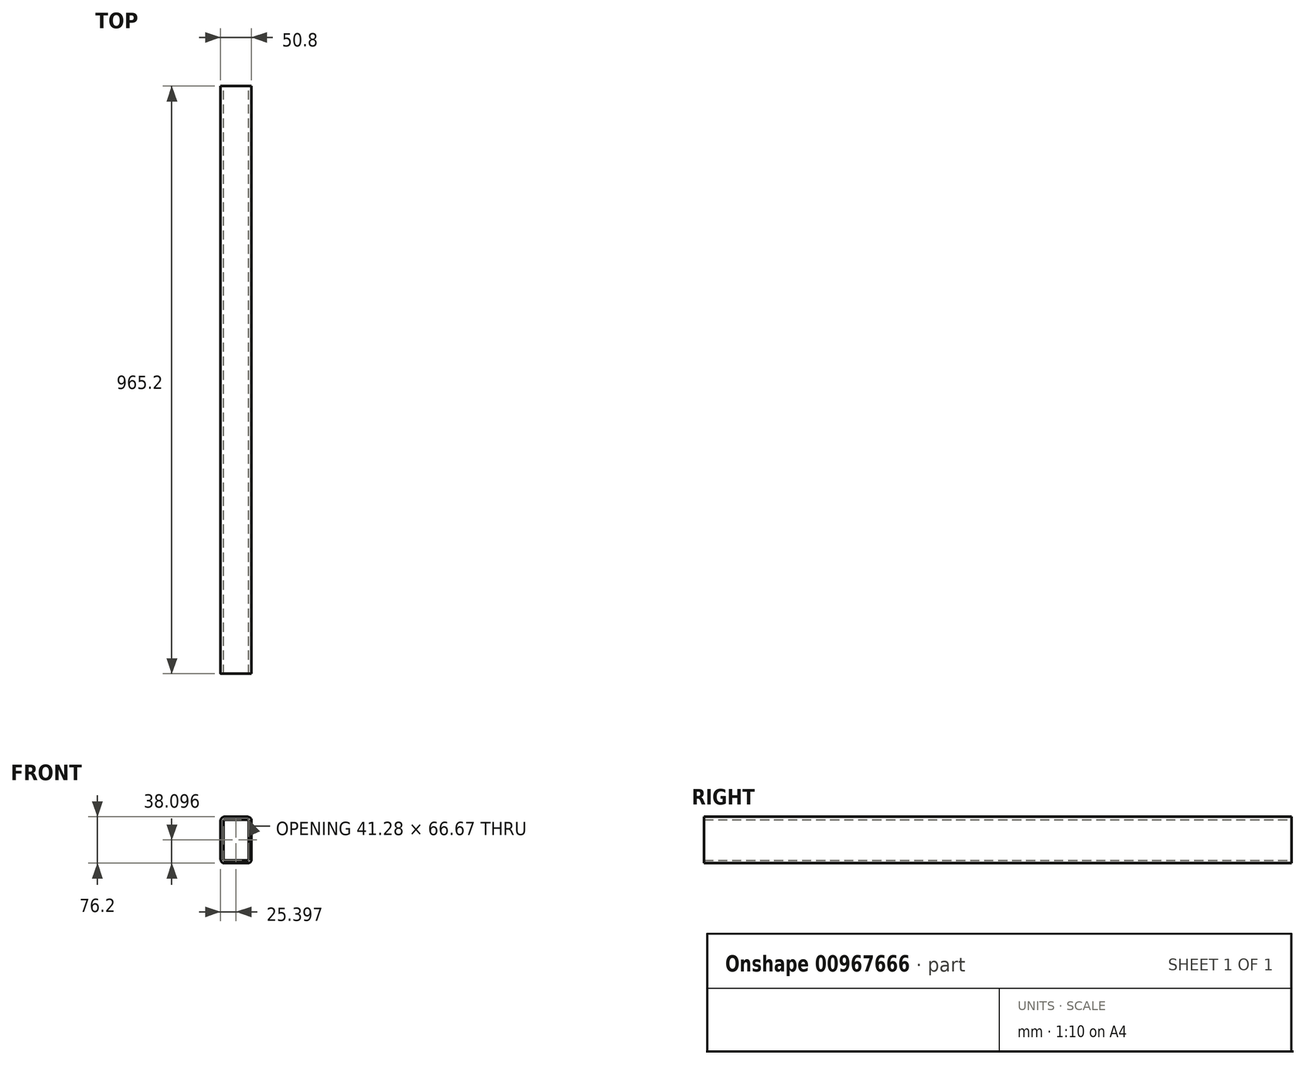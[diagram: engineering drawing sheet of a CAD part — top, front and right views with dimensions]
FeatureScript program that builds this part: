
annotation { "Feature Type Name" : "Feature", "Feature Type Description" : "" }
export const myFeature = defineFeature(function(context is Context, id is Id, definition is map)
    precondition{}
    {
        {
            var Q0;
            Q0=qCreatedBy(makeId("Front.planeOp"),FACE);
            var sketch = newSketch(context, id + "F0", { "sketchPlane" : qUnion([Q0])});
            skLineSegment(sketch, "E0.bottom", {"start": v(-19.28, -38.02) * mm, "end": v(18.82, -38.02) * mm});
            skLineSegment(sketch, "E0.top", {"start": v(-19.28, 38.18) * mm, "end": v(18.82, 38.18) * mm});
            skLineSegment(sketch, "E0.left", {"start": v(-25.63, -31.67) * mm, "end": v(-25.63, 31.83) * mm});
            skLineSegment(sketch, "E0.right", {"start": v(25.17, -31.67) * mm, "end": v(25.17, 31.83) * mm});
            skPoint(sketch, "E1.visualSharp", {"position": v(-25.63, 38.18) * mm});
            skArc(sketch, "E1.filletArc", {"start": v(-19.28, 38.18) * mm, "mid": v(-23.77, 36.32) * mm, "end": v(-25.63, 31.83) * mm});
            skPoint(sketch, "E2.visualSharp", {"position": v(25.17, 38.18) * mm});
            skArc(sketch, "E2.filletArc", {"start": v(25.17, 31.83) * mm, "mid": v(23.3, 36.32) * mm, "end": v(18.82, 38.18) * mm});
            skPoint(sketch, "E3.visualSharp", {"position": v(25.17, -38.02) * mm});
            skArc(sketch, "E3.filletArc", {"start": v(18.82, -38.02) * mm, "mid": v(23.3, -36.16) * mm, "end": v(25.17, -31.67) * mm});
            skPoint(sketch, "E4.visualSharp", {"position": v(-25.63, -38.02) * mm});
            skArc(sketch, "E4.filletArc", {"start": v(-25.63, -31.67) * mm, "mid": v(-23.77, -36.16) * mm, "end": v(-19.28, -38.02) * mm});
            skArc(sketch, "E5.0", {"start": v(-19.28, 33.41) * mm, "mid": v(-20.4, 32.95) * mm, "end": v(-20.87, 31.83) * mm});
            skLineSegment(sketch, "E5.1", {"start": v(-20.87, -31.67) * mm, "end": v(-20.87, 31.83) * mm});
            skLineSegment(sketch, "E5.2", {"start": v(-19.28, 33.41) * mm, "end": v(18.82, 33.41) * mm});
            skArc(sketch, "E5.3", {"start": v(-20.87, -31.67) * mm, "mid": v(-20.4, -32.8) * mm, "end": v(-19.28, -33.26) * mm});
            skArc(sketch, "E5.4", {"start": v(20.4, 31.83) * mm, "mid": v(19.94, 32.95) * mm, "end": v(18.82, 33.41) * mm});
            skLineSegment(sketch, "E5.5", {"start": v(20.4, -31.67) * mm, "end": v(20.4, 31.83) * mm});
            skArc(sketch, "E5.6", {"start": v(18.82, -33.26) * mm, "mid": v(19.94, -32.8) * mm, "end": v(20.4, -31.67) * mm});
            skLineSegment(sketch, "E5.7", {"start": v(-19.28, -33.26) * mm, "end": v(18.82, -33.26) * mm});
            skSolve(sketch);
        }
        {
            var Q0;
            Q0 = qSketchRegion(id + "F0", true);
            extrude(context, id + "F1", {"entities" : qUnion([Q0]), "depth" : 965.2 * mm, "offsetDistance" : 25.4 * mm});
        }
    });
